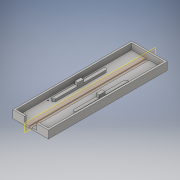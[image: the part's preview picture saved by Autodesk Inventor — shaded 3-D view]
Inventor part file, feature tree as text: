
AUTODESK INVENTOR PART (.ipt)
format: ipt  version: 2016 (Build 200138000, 138)  size: 193,536 bytes
history: native  units: mm
features: sketch x6, extrude x4, other x2, imported_body x1, hole x1, chamfer x1, mirror x1, projected_geometry x1
ambient origin geometry x8: Origin, YZ Plane, XZ Plane, XY Plane, X Axis, Y Axis, Z Axis, Center Point
bodies: Solid1 (feature_tree)
feature tree (17):
  imported_body  "Base"
  other  "<userpath>\Documents\GitHub\3D\Hoja Oculta\Parametros.xlsx"
  extrude  "Paredes"  Depth=200.0mm
  extrude  "Canal"  Depth=3.0mm
  hole  "Agujeros"  [1 undecoded]
  other  "Mitad"
  extrude  "Soporte base"  Depth=1.5mm TaperAngle=0.0deg
  chamfer  "Chaflán soporte"  Distance=50.0mm
  extrude  "Soporte tope"  Depth=5.0mm
  mirror  "Segundo soporte"
  sketch  "Sketch1"  dims[d0=60.0mm d1=200.0mm]
  sketch  "Sketch4"  dims[d2=3.0mm d3=0.0mm d6=3.0mm]
  projected_geometry  "Projected Loop2"
  sketch  "Sketch5"  dims[d7=20.6mm d8=10.0mm d9=0.0mm]
  sketch  "Sketch6"  dims[d10=5.0mm d11=1.5mm d12=0.0mm]
  sketch  "Sketch9"  dims[d13=3.5mm]
  sketch  "Sketch10"  dims[d14=50.0mm d15=50.0mm d16=2.0mm d17=6.0mm d18=4.0mm d19=2.0mm d20=90.0deg d21=50.0mm d22=20.594885mm d23=15.3mm d24=90.0mm d25=5.0mm d26=4.0mm d27=0.0mm d28=2.5mm d29=2.0mm d30=45.0deg d31=10.0mm d32=5.0mm d33=0.0mm]
note: 1 required parameter value undecoded (feature->parameter linkage not recoverable at this tier; creation-order binding heuristic only, values carry confidence <= 0.55)
